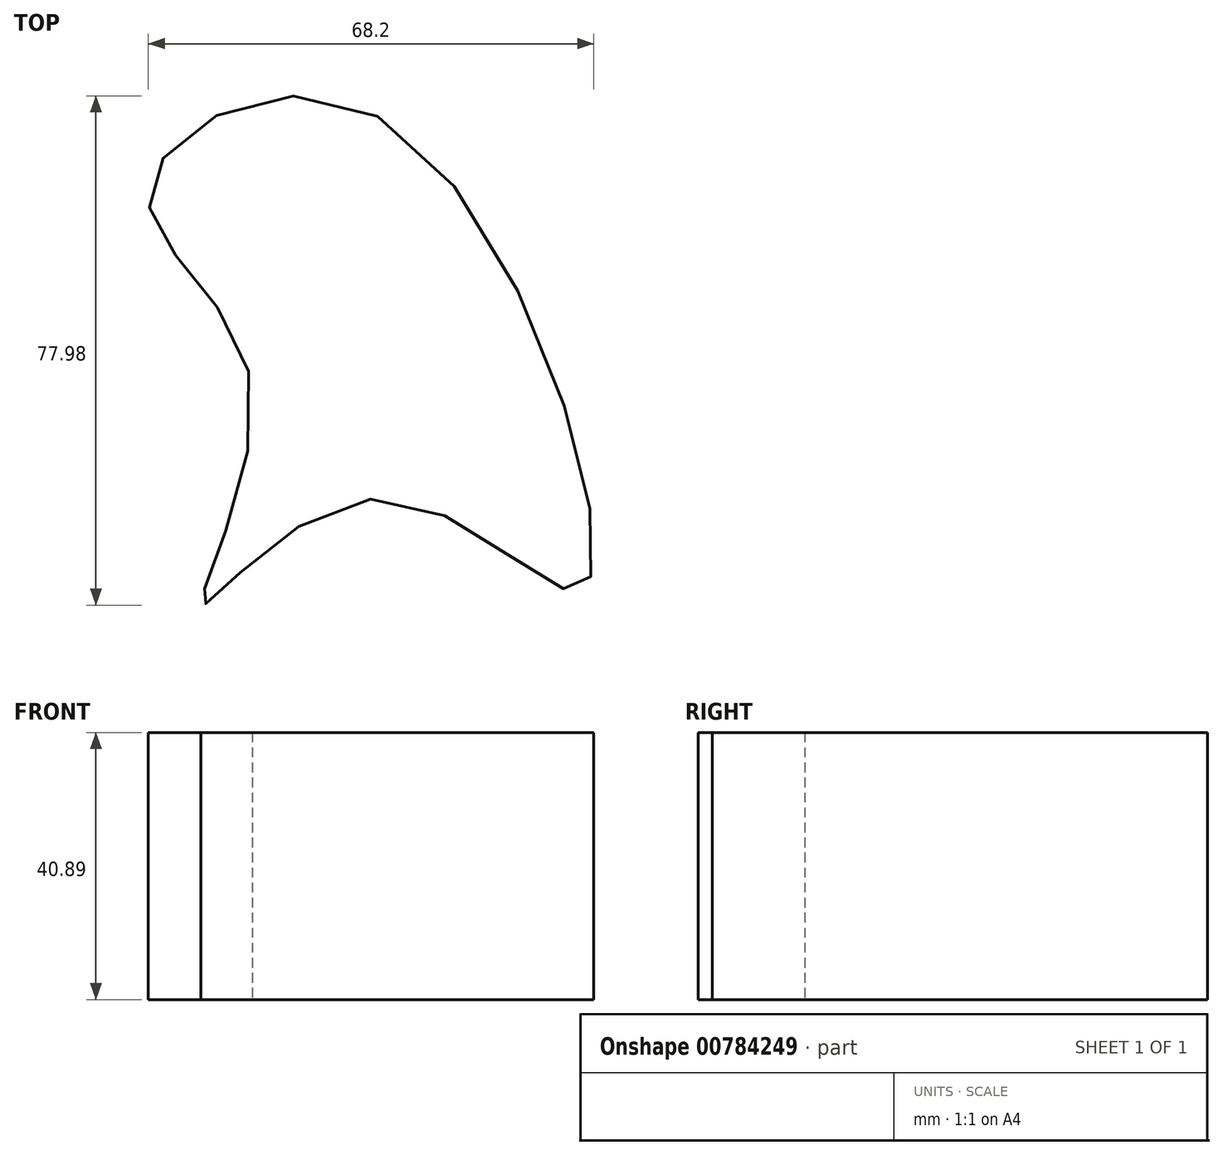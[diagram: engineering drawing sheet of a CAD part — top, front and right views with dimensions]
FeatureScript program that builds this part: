
annotation { "Feature Type Name" : "Feature", "Feature Type Description" : "" }
export const myFeature = defineFeature(function(context is Context, id is Id, definition is map)
    precondition{}
    {
        {
            var Q0;
            Q0=qCreatedBy(makeId("Top.planeOp"),FACE);
            var sketch = newSketch(context, id + "F0", { "sketchPlane" : qUnion([Q0])});
            skFitSpline(sketch, "E0", {"points": [v(0, 40.57) * mm, v(-35.01, 29.09) * mm, v(-19.45, 0) * mm, v(-26.86, -34.27) * mm, v(0, -17.97) * mm, v(31.68, -31.68) * mm, v(0, 40.57) * mm]});
            skSolve(sketch);
        }
        {
            var Q0;
            Q0=makeQuery(id+"F0.imprint","IMPRINT",FACE,{"disambiguationData":[TD([[makeQuery(id+"F0.imprint","IMPRINT",EDGE,{"derivedFrom":sQuery(id+"F0.wireOp",EDGE,"E0")}),1.0]])]});
            extrude(context, id + "F1", {"entities" : qUnion([Q0]), "depth" : 40.9 * mm, "offsetDistance" : 25.4 * mm});
        }
    });
